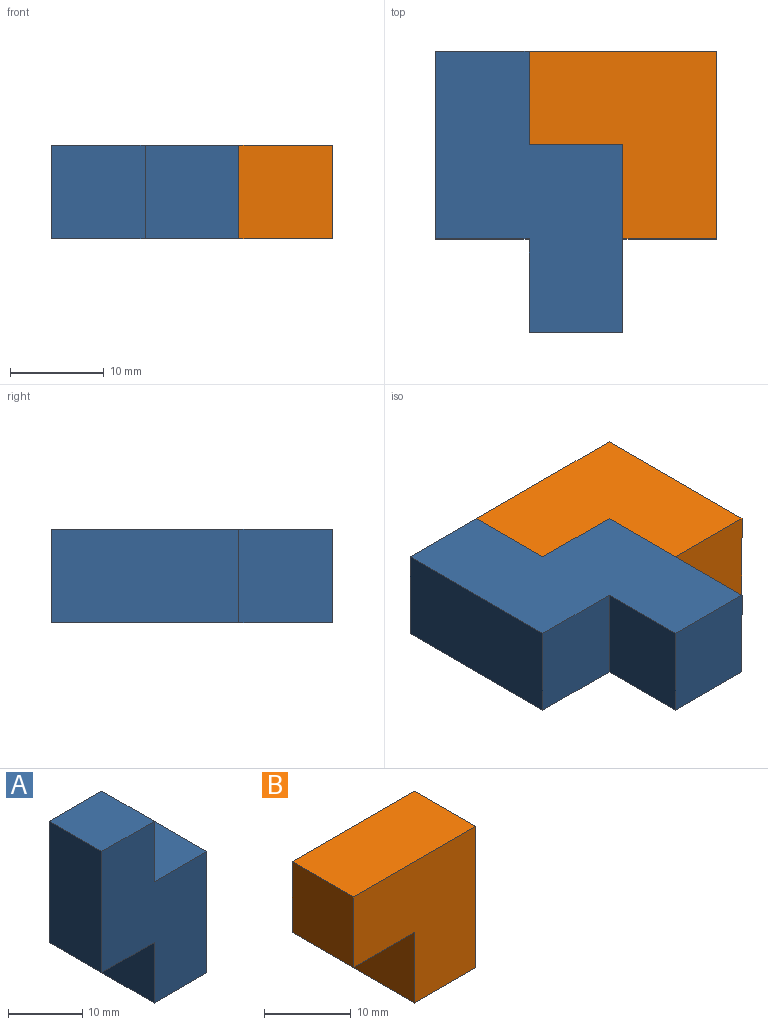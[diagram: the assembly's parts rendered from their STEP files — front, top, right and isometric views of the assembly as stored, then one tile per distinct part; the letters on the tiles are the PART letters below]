
ASSEMBLY  parts=2 mates=1
PART A: 10 faces, bbox 20x10x30 mm
  f0: plane 20x10mm, normal (1,0,0), area 200mm2, adj f1,f6,f7,f9
  f1: plane 10x10mm, normal (0,0,-1), area 100mm2, adj f0,f5,f6,f7
  f2: plane 10x10mm, normal (0,0,1), area 100mm2, adj f3,f6,f7,f8
  f3: plane 20x10mm, normal (-1,0,0), area 200mm2, adj f2,f4,f6,f7
  f4: plane 10x10mm, normal (0,0,-1), area 100mm2, adj f3,f5,f6,f7
  f5: plane 10x10mm, normal (-1,0,0), area 100mm2, adj f1,f4,f6,f7
  f6: plane 30x20mm, normal (0,-1,0), area 400mm2, adj f0,f1,f2,f3,f4,f5,f8,f9
  f7: plane 30x20mm, normal (0,1,0), area 400mm2, adj f0,f1,f2,f3,f4,f5,f8,f9
  f8: plane 10x10mm, normal (1,0,0), area 100mm2, adj f2,f6,f7,f9
  f9: plane 10x10mm, normal (0,0,1), area 100mm2, adj f0,f6,f7,f8
PART B: 8 faces, bbox 20x10x20 mm
  f0: plane 20x20mm, normal (0,-1,0), area 300mm2, adj f1,f3,f4,f5,f6,f7
  f1: plane 10x10mm, normal (0,0,-1), area 100mm2, adj f0,f2,f5,f6
  f2: plane 20x20mm, normal (0,1,0), area 300mm2, adj f1,f3,f4,f5,f6,f7
  f3: plane 20x10mm, normal (0,0,1), area 200mm2, adj f0,f2,f4,f5
  f4: plane 20x10mm, normal (1,0,0), area 200mm2, adj f0,f2,f3,f7
  f5: plane 10x10mm, normal (-1,0,0), area 100mm2, adj f0,f1,f2,f3
  f6: plane 10x10mm, normal (-1,0,0), area 100mm2, adj f0,f1,f2,f7
  f7: plane 10x10mm, normal (0,0,-1), area 100mm2, adj f0,f2,f4,f6
PLACE A rot(axis=(-1,0,0),90deg) t=(-7.87,-24.41,2.2)mm fixed
PLACE B rot(axis=(-1,0,0),90deg) t=(-7.87,-24.41,2.2)mm
MATE fastened A.f8 <-> B.f5  axis (1,0,0) through (-17.87,0.59,7.2)mm
